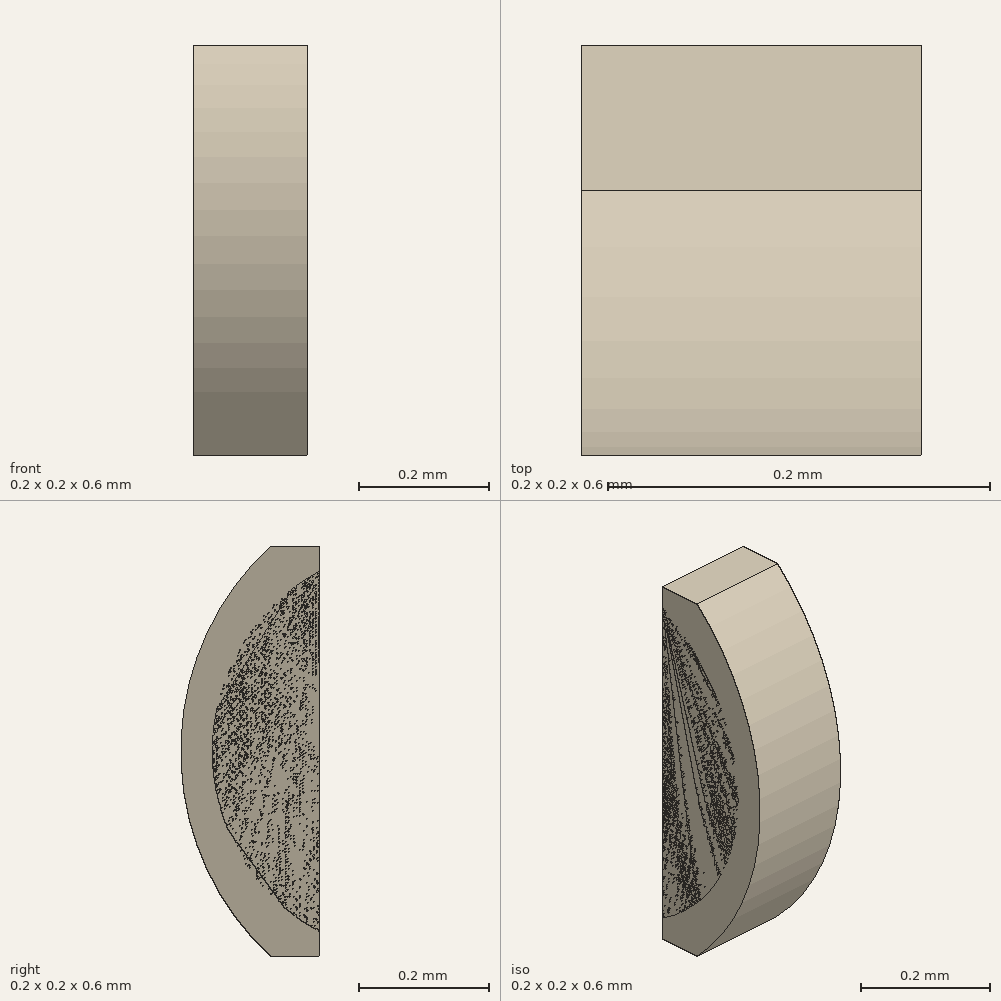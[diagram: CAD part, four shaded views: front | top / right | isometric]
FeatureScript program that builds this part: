
annotation { "Feature Type Name" : "Feature", "Feature Type Description" : "" }
export const myFeature = defineFeature(function(context is Context, id is Id, definition is map)
    precondition{}
    {
        {
            var Q0;
            Q0=qCreatedBy(makeId("Front.planeOp"),FACE);
            var sketch = newSketch(context, id + "F0", { "sketchPlane" : qUnion([Q0])});
            skLineSegment(sketch, "E0.bottom", {"start": v(0.09, 0.32) * mm, "end": v(-0.09, 0.32) * mm});
            skLineSegment(sketch, "E0.top", {"start": v(0.09, -0.32) * mm, "end": v(-0.09, -0.32) * mm});
            skLineSegment(sketch, "E0.left", {"start": v(0.09, 0.32) * mm, "end": v(0.09, -0.32) * mm});
            skLineSegment(sketch, "E0.right", {"start": v(-0.09, 0.32) * mm, "end": v(-0.09, -0.32) * mm});
            skPoint(sketch, "E0.middle", {"position": v(0, 0) * mm});
            skLineSegment(sketch, "E1.bottom", {"start": v(-0.09, -0.67) * mm, "end": v(0.09, -0.67) * mm});
            skLineSegment(sketch, "E1.top", {"start": v(-0.09, -1.3) * mm, "end": v(0.09, -1.3) * mm});
            skLineSegment(sketch, "E1.left", {"start": v(-0.09, -0.67) * mm, "end": v(-0.09, -1.3) * mm});
            skLineSegment(sketch, "E1.right", {"start": v(0.09, -0.67) * mm, "end": v(0.09, -1.3) * mm});
            skSolve(sketch);
        }
        {
            var Q0;
            Q0=qCreatedBy(makeId("Right.planeOp"),FACE);
            var sketch = newSketch(context, id + "F1", { "sketchPlane" : qUnion([Q0])});
            skLineSegment(sketch, "E2.bottom", {"start": v(0, 0.32) * mm, "end": v(0.08, 0.32) * mm});
            skLineSegment(sketch, "E2.top", {"start": v(0, -0.32) * mm, "end": v(0.08, -0.32) * mm});
            skLineSegment(sketch, "E2.left", {"start": v(0, 0.32) * mm, "end": v(0, -0.32) * mm, "construction": true});
            skLineSegment(sketch, "E2.right", {"start": v(0.08, 0.32) * mm, "end": v(0.08, -0.32) * mm});
            skLineSegment(sketch, "E3.bottom", {"start": v(0, -0.67) * mm, "end": v(0.08, -0.67) * mm});
            skLineSegment(sketch, "E3.top", {"start": v(0, -1.3) * mm, "end": v(0.08, -1.3) * mm});
            skLineSegment(sketch, "E3.left", {"start": v(0, -0.67) * mm, "end": v(0, -1.3) * mm, "construction": true});
            skLineSegment(sketch, "E3.right", {"start": v(0.08, -0.67) * mm, "end": v(0.08, -1.3) * mm});
            skCircle(sketch, "E4", {"center": v(0.3, 0) * mm, "radius": 0.43 * mm});
            skCircle(sketch, "E5", {"center": v(0.3, -0.98) * mm, "radius": 0.43 * mm});
            skPoint(sketch, "E5.centerSnap0", {"position": v(0, -0.98) * mm});
            skSolve(sketch);
        }
        {
            var Q0;
            {var subQ0=sQuery(id+"F1.wireOp",EDGE,"E2.right");Q0=makeQuery(id+"F1.imprint","IMPRINT",FACE,{"disambiguationData":[TD([[makeQuery(id+"F1.imprint","IMPRINT",EDGE,{"derivedFrom":subQ0}),-1.0]])]});}
            extrude(context, id + "F2", {"entities" : qUnion([Q0]), "depth" : 0.18 * mm, "symmetric" : true});
        }
        {
            var Q0;
            Q0=qCreatedBy(makeId("Front.planeOp"),FACE);
            var sketch = newSketch(context, id + "F3", { "sketchPlane" : qUnion([Q0])});
            skLineSegment(sketch, "E6.bottom", {"start": v(0.09, 0.28) * mm, "end": v(-0.09, 0.28) * mm});
            skLineSegment(sketch, "E6.top", {"start": v(0.09, -0.28) * mm, "end": v(-0.09, -0.28) * mm});
            skLineSegment(sketch, "E6.left", {"start": v(0.09, 0.28) * mm, "end": v(0.09, -0.28) * mm});
            skLineSegment(sketch, "E6.right", {"start": v(-0.09, 0.28) * mm, "end": v(-0.09, -0.28) * mm});
            skPoint(sketch, "E6.middle", {"position": v(0, 0) * mm});
            skSolve(sketch);
        }
        {
            var Q0;
            Q0=qCreatedBy(makeId("Right.planeOp"),FACE);
            var sketch = newSketch(context, id + "F4", { "sketchPlane" : qUnion([Q0])});
            skLineSegment(sketch, "E7.bottom", {"start": v(0, 0.28) * mm, "end": v(0.08, 0.28) * mm, "construction": true});
            skLineSegment(sketch, "E7.top", {"start": v(0, -0.28) * mm, "end": v(0.08, -0.28) * mm, "construction": true});
            skLineSegment(sketch, "E7.left", {"start": v(0, 0.28) * mm, "end": v(0, -0.28) * mm, "construction": true});
            skLineSegment(sketch, "E7.right", {"start": v(0.08, 0.28) * mm, "end": v(0.08, -0.28) * mm});
            skCircle(sketch, "E8", {"center": v(0.23, 0) * mm, "radius": 0.32 * mm});
            skSolve(sketch);
        }
        {
            var Q0;
            {var subQ0=sQuery(id+"F4.wireOp",EDGE,"E7.right");Q0=makeQuery(id+"F4.imprint","IMPRINT",FACE,{"disambiguationData":[TD([[makeQuery(id+"F4.imprint","IMPRINT",EDGE,{"derivedFrom":subQ0}),-1.0]])]});}
            extrude(context, id + "F5", {"entities" : qUnion([Q0]), "depth" : 0.18 * mm, "symmetric" : true});
        }
    });
